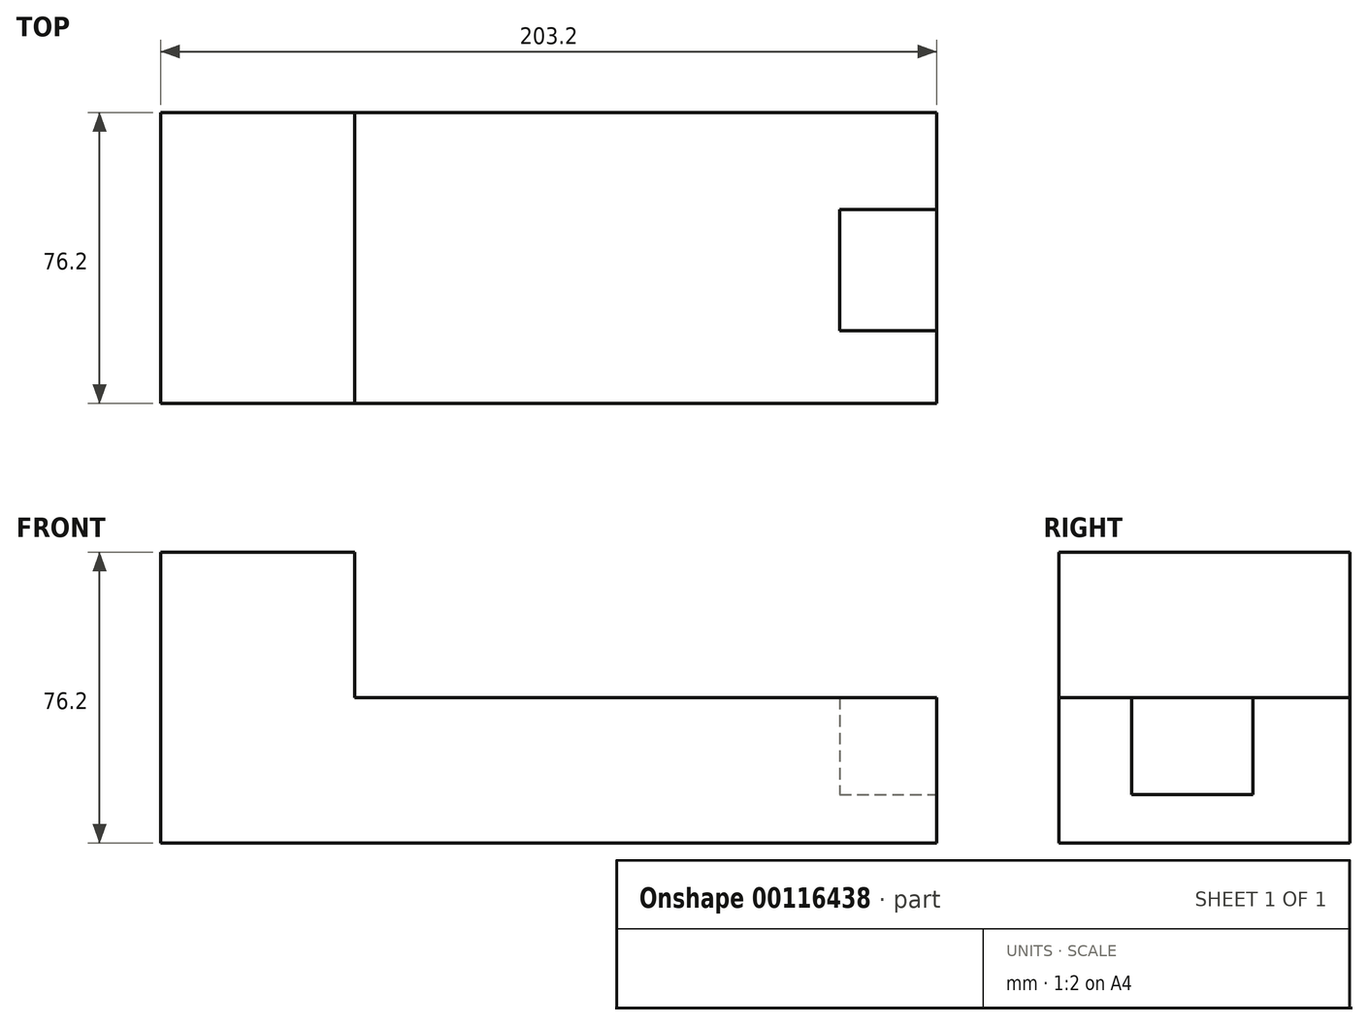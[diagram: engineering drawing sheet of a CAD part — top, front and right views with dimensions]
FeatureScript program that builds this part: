
annotation { "Feature Type Name" : "Feature", "Feature Type Description" : "" }
export const myFeature = defineFeature(function(context is Context, id is Id, definition is map)
    precondition{}
    {
        {
            var Q0;
            Q0=qCreatedBy(makeId("Front.planeOp"),FACE);
            var sketch = newSketch(context, id + "F0", { "sketchPlane" : qUnion([Q0])});
            skLineSegment(sketch, "E0", {"start": v(0, 0) * mm, "end": v(0, 76.2) * mm});
            skLineSegment(sketch, "E1", {"start": v(0, 76.2) * mm, "end": v(50.8, 76.2) * mm});
            skLineSegment(sketch, "E2", {"start": v(50.8, 76.2) * mm, "end": v(50.8, 38.1) * mm});
            skLineSegment(sketch, "E3", {"start": v(50.8, 38.1) * mm, "end": v(203.2, 38.1) * mm});
            skLineSegment(sketch, "E4", {"start": v(203.2, 38.1) * mm, "end": v(203.2, 0) * mm});
            skLineSegment(sketch, "E5", {"start": v(203.2, 0) * mm, "end": v(0, 0) * mm});
            skSolve(sketch);
        }
        {
            var Q0;
            Q0=makeQuery(id+"F0.imprint","IMPRINT",FACE,{"disambiguationData":[TD([[makeQuery(id+"F0.imprint","IMPRINT",EDGE,{"derivedFrom":sQuery(id+"F0.wireOp",EDGE,"E0")}),-1.0]])]});
            extrude(context, id + "F1", {"entities" : qUnion([Q0]), "depth" : 76.2 * mm});
        }
        {
            var Q0;
            Q0=makeQuery(id+"F1.opExtrude","SWEPT_FACE",FACE,{"disambiguationData":[OSD([sQuery(id+"F0.wireOp",EDGE,"E4")])]});
            var sketch = newSketch(context, id + "F2", { "sketchPlane" : qUnion([Q0])});
            skLineSegment(sketch, "E6.bottom", {"start": v(-57.15, 38.1) * mm, "end": v(-25.37, 38.1) * mm});
            skLineSegment(sketch, "E6.top", {"start": v(-57.15, 12.7) * mm, "end": v(-25.37, 12.7) * mm});
            skLineSegment(sketch, "E6.left", {"start": v(-57.15, 38.1) * mm, "end": v(-57.15, 12.7) * mm});
            skLineSegment(sketch, "E6.right", {"start": v(-25.37, 38.1) * mm, "end": v(-25.37, 12.7) * mm});
            skSolve(sketch);
        }
        {
            var Q0;
            Q0=makeQuery(id+"F2.imprint","IMPRINT",FACE,{"disambiguationData":[TD([[makeQuery(id+"F2.imprint","IMPRINT",EDGE,{"derivedFrom":sQuery(id+"F2.wireOp",EDGE,"E6.bottom")}),-1.0]])]});
            extrude(context, id + "F3", {"entities" : qUnion([Q0]), "operationType" : NewBodyOperationType.REMOVE, "oppositeDirection" : true, "depth" : 25.4 * mm});
        }
    });
